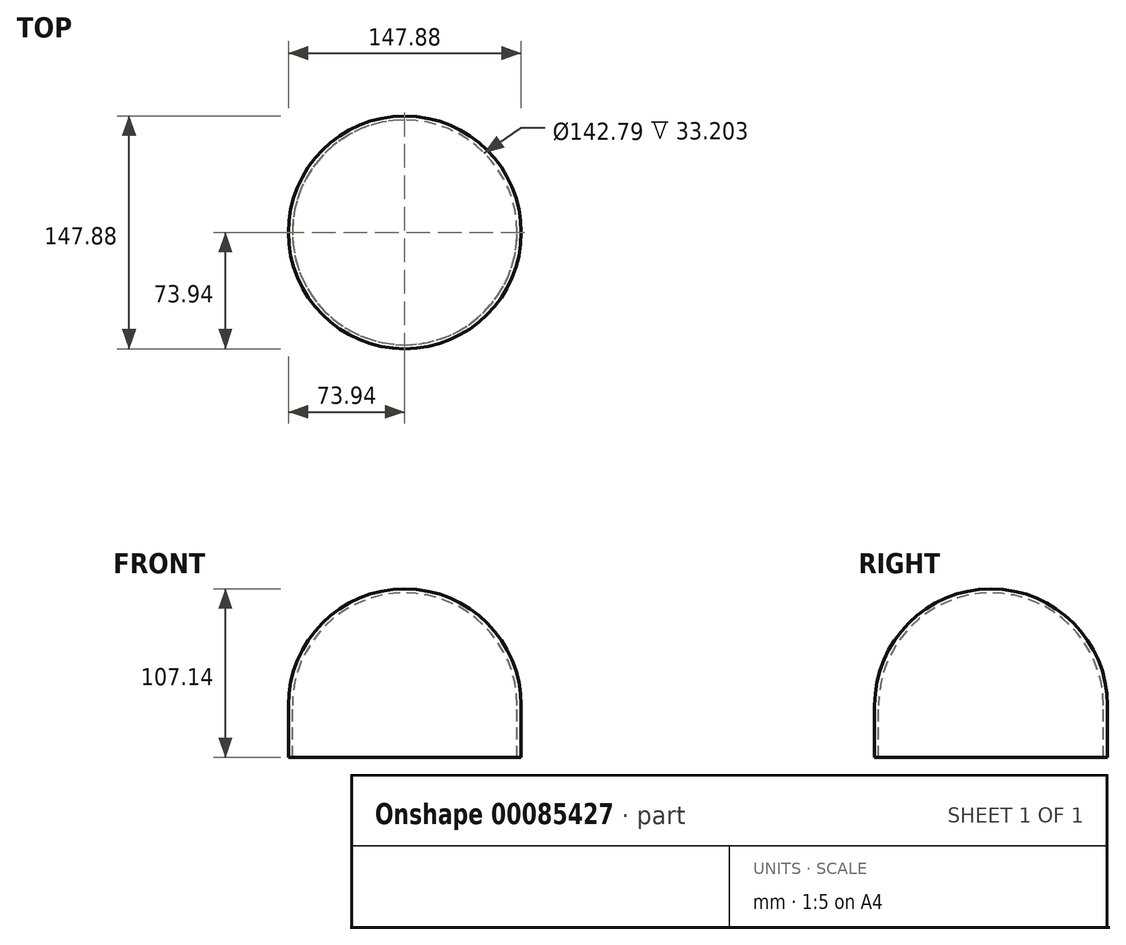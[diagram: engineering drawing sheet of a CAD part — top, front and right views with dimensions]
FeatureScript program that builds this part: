
annotation { "Feature Type Name" : "Feature", "Feature Type Description" : "" }
export const myFeature = defineFeature(function(context is Context, id is Id, definition is map)
    precondition{}
    {
        {
            var Q0;
            Q0=qCreatedBy(makeId("Top.planeOp"),FACE);
            var sketch = newSketch(context, id + "F0", { "sketchPlane" : qUnion([Q0])});
            skArc(sketch, "E0", {"start": v(0, 73.94) * mm, "mid": v(-73.94, 0) * mm, "end": v(0, -73.94) * mm});
            skLineSegment(sketch, "E1", {"start": v(0, 73.94) * mm, "end": v(0, -73.94) * mm});
            skSolve(sketch);
        }
        {
            var Q0;
            Q0 = qSketchRegion(id + "F0", true);
            var Q1;
            Q1=sQuery(id+"F0.wireOp",EDGE,"E1");
            revolve(context, id + "F1", {"entities" : qUnion([Q0]), "axis" : qUnion([Q1]), "revolveType" : RevolveType.ONE_DIRECTION, "angle" : 351.9 * degree});
        }
        {
            var Q0;
            Q0=makeQuery(id+"F1.opRevolve","CAP_FACE",FACE,{"disambiguationData":[OSD([sQuery(id+"F0.wireOp",EDGE,"E0"),sQuery(id+"F0.wireOp",EDGE,"E1")])],"isStart":false});
            var sketch = newSketch(context, id + "F2", { "sketchPlane" : qUnion([Q0])});
            skArc(sketch, "E2.0", {"start": v(0, -71.4) * mm, "mid": v(-71.4, 0) * mm, "end": v(0, 71.4) * mm});
            skArc(sketch, "E2.1", {"start": v(0, -73.94) * mm, "mid": v(-73.94, 0) * mm, "end": v(0, 73.94) * mm});
            skLineSegment(sketch, "E2.2", {"start": v(0, 71.4) * mm, "end": v(0, 73.94) * mm});
            skLineSegment(sketch, "E2.3", {"start": v(0, -73.94) * mm, "end": v(0, -71.4) * mm});
            skLineSegment(sketch, "E3", {"start": v(0, -73.94) * mm, "end": v(0, 73.94) * mm});
            skSolve(sketch);
        }
        {
            var Q0;
            Q0 = qSketchRegion(id + "F2", true);
            var Q1;
            Q1=sQuery(id+"F2.wireOp",EDGE,"E3");
            revolve(context, id + "F3", {"operationType" : NewBodyOperationType.ADD, "entities" : qUnion([Q0]), "axis" : qUnion([Q1]), "revolveType" : RevolveType.FULL});
        }
        {
            var Q0;
            Q0=qCreatedBy(makeId("Top.planeOp"),FACE);
            var sketch = newSketch(context, id + "F4", { "sketchPlane" : qUnion([Q0])});
            skLineSegment(sketch, "E4.bottom", {"start": v(-122.71, 185.83) * mm, "end": v(122.71, 185.83) * mm});
            skLineSegment(sketch, "E4.top", {"start": v(-122.71, -185.83) * mm, "end": v(122.71, -185.83) * mm});
            skLineSegment(sketch, "E4.left", {"start": v(-122.71, 185.83) * mm, "end": v(-122.71, -185.83) * mm});
            skLineSegment(sketch, "E4.right", {"start": v(122.71, 185.83) * mm, "end": v(122.71, -185.83) * mm});
            skPoint(sketch, "E4.middle", {"position": v(0, 0) * mm});
            skSolve(sketch);
        }
        {
            var Q0;
            Q0 = qSketchRegion(id + "F4", true);
            extrude(context, id + "F5", {"entities" : qUnion([Q0]), "operationType" : NewBodyOperationType.REMOVE, "oppositeDirection" : true, "depth" : 95.05 * mm});
        }
        {
            var Q0;
            Q0=makeQuery(id+"F5.boolean.opBoolean","COPY",FACE,{"derivedFrom":makeQuery(id+"F5.opExtrude","CAP_FACE",FACE,{"disambiguationData":[OSD([sQuery(id+"F4.wireOp",EDGE,"E4.bottom"),sQuery(id+"F4.wireOp",EDGE,"E4.top"),sQuery(id+"F4.wireOp",EDGE,"E4.left"),sQuery(id+"F4.wireOp",EDGE,"E4.right")])],"isStart":true})});
            shell(context, id + "F6", {"entities" : qUnion([Q0]), "thickness" : 2.54 * mm});
        }
        {
            var Q0;
            Q0=makeQuery(id+"F5.boolean.opBoolean","COPY",FACE,{"derivedFrom":makeQuery(id+"F5.opExtrude","CAP_FACE",FACE,{"disambiguationData":[OSD([sQuery(id+"F4.wireOp",EDGE,"E4.bottom"),sQuery(id+"F4.wireOp",EDGE,"E4.top"),sQuery(id+"F4.wireOp",EDGE,"E4.left"),sQuery(id+"F4.wireOp",EDGE,"E4.right")])],"isStart":true})});
            extrude(context, id + "F7", {"entities" : qUnion([Q0]), "operationType" : NewBodyOperationType.ADD, "depth" : 33.2 * mm});
        }
    });
